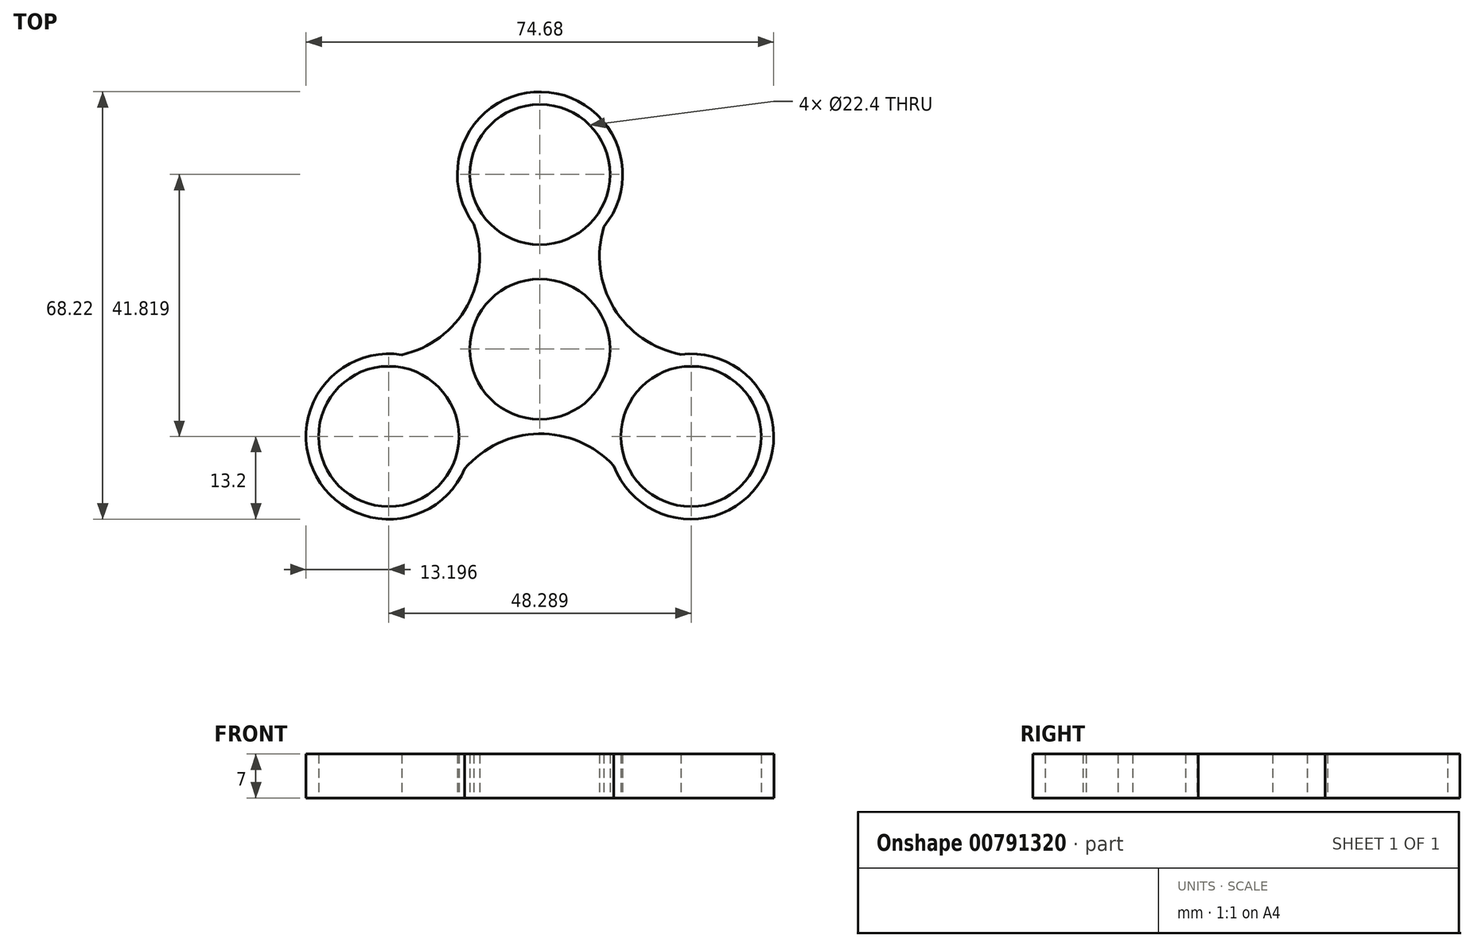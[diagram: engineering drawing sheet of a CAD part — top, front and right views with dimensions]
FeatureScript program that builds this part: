
annotation { "Feature Type Name" : "Feature", "Feature Type Description" : "" }
export const myFeature = defineFeature(function(context is Context, id is Id, definition is map)
    precondition{}
    {
        {
            var Q0;
            Q0=qCreatedBy(makeId("Top.planeOp"),FACE);
            var sketch = newSketch(context, id + "F0", { "sketchPlane" : qUnion([Q0])});
            skCircle(sketch, "E0", {"center": v(0, 0) * mm, "radius": 11.2 * mm});
            skCircle(sketch, "E1", {"center": v(0, 27.88) * mm, "radius": 11.2 * mm});
            skCircle(sketch, "E2.1.0", {"center": v(-24.14, -13.94) * mm, "radius": 11.2 * mm});
            skCircle(sketch, "E2.2.0", {"center": v(24.14, -13.94) * mm, "radius": 11.2 * mm});
            skCircle(sketch, "E3", {"center": v(0, 27.88) * mm, "radius": 13.2 * mm});
            skCircle(sketch, "E4.1.0", {"center": v(-24.14, -13.94) * mm, "radius": 13.2 * mm});
            skCircle(sketch, "E4.2.0", {"center": v(24.14, -13.94) * mm, "radius": 13.2 * mm});
            skCircle(sketch, "E5", {"center": v(0, 0) * mm, "radius": 13.2 * mm});
            skArc(sketch, "E6", {"start": v(10.23, 19.54) * mm, "mid": v(11.8, 6.58) * mm, "end": v(22.54, -0.84) * mm});
            skArc(sketch, "E7.1.0", {"start": v(-22.04, -0.9) * mm, "mid": v(-11.6, 6.93) * mm, "end": v(-10.54, 19.94) * mm});
            skArc(sketch, "E7.2.0", {"start": v(11.8, -18.63) * mm, "mid": v(-0.2, -13.51) * mm, "end": v(-12, -19.1) * mm});
            skSolve(sketch);
        }
        {
            var Q0;
            Q0=makeQuery(id+"F0.imprint","IMPRINT",FACE,{"disambiguationData":[TD([[makeQuery(id+"F0.imprint","IMPRINT",EDGE,{"derivedFrom":sQuery(id+"F0.wireOp",EDGE,"E1")}),-1.0]])]});
            var Q1;
            Q1=makeQuery(id+"F0.imprint","IMPRINT",FACE,{"disambiguationData":[TD([[makeQuery(id+"F0.imprint","IMPRINT",EDGE,{"derivedFrom":sQuery(id+"F0.wireOp",EDGE,"E2.1.0")}),-1.0]])]});
            var Q2;
            Q2=makeQuery(id+"F0.imprint","IMPRINT",FACE,{"disambiguationData":[TD([[makeQuery(id+"F0.imprint","IMPRINT",EDGE,{"derivedFrom":sQuery(id+"F0.wireOp",EDGE,"E2.2.0")}),-1.0]])]});
            var Q3;
            Q3=makeQuery(id+"F0.imprint","IMPRINT",FACE,{"disambiguationData":[TD([[makeQuery(id+"F0.imprint","IMPRINT",EDGE,{"derivedFrom":sQuery(id+"F0.wireOp",EDGE,"E5")}),-1.0]])]});
            var Q4;
            Q4=makeQuery(id+"F0.imprint","IMPRINT",FACE,{"disambiguationData":[TD([[makeQuery(id+"F0.imprint","IMPRINT",EDGE,{"derivedFrom":sQuery(id+"F0.wireOp",EDGE,"E0")}),-1.0]])]});
            extrude(context, id + "F1", {"entities" : qUnion([Q0, Q1, Q2, Q3, Q4]), "depth" : 7 * mm, "offsetDistance" : 25 * mm});
        }
    });
